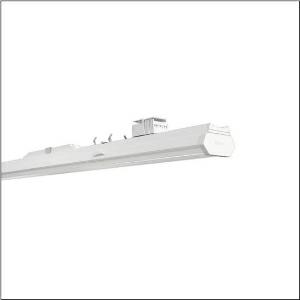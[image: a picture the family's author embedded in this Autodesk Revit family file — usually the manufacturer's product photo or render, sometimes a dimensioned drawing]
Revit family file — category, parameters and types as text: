
# Revit family: licross_r__21_protected_mo_52td11cn49xg_2815
name_source: partatom
category: Lighting Fixtures
units: mm (PartAtom-declared; Revit-internal decimal feet)

## family parameters
Cut with Voids When Loaded = No
Host = Face
Light Source = No
Part Type = Normal
Room Calculation Point = No
Round Connector Dimension = Use Diameter
Shared = No

## types (1)
- --- (1 x LED, 9070 lm, 50.4 W, 4000K)
    Apparent Load = 50 VA
    CIE Flux Codes = 83 94 98 100 100
    Color Rendering = 80
    Color Temperature = 4000K
    Default Elevation = 1800 mm
    Description = Licross® 21 Protected MO, luminaire insert, of sheet steel, galvanised, coil coated, white, length: 1.500mm, width: 90mm, height: 103mm, LED rated luminous flux: 9.080lm, light colour: 840, control gear: ON/OFF Multilumen, CLOi, control gear: ECG Multilumen, with plug, 3-pole, with phase selection, mains connection: 220..240V, AC, 50/60Hz, start of lifetime: 50W, end of service life: 61W, internal wiring halogen-free, primary light control with lens, of plastic, primary optical cover: cover, of PMMA, light emission: direct distribution, primary light characteristic: symmetric, protection rating (complete): IP54, insulation class (complete): insulation class I (protective earthing), certification: CE, ENEC, VDE, UKCA, protection symbol: D if used in an environment with non-conductive dust loads with corresponding accessories, impact resistance: IK06, permissible ambient temperature for indoor applications: -35..+45°C, corresponds to IFS (International Featured Standards) requirements for safety and quality in the food industry, reducing of maximum allowable ambient temperature of 5°C with ceiling mounting, LABS conformity tested according to VDMA 24364:2018-05, packaging unit: 1 piece
    Height = 92 mm
    Lamp = 1 x LED
    Lamp Light Flux = 9070 lm
    Lamp Power = 50.4 W
    Lamp count = 1
    Length = 1500 mm
    Luminous efficacy = 180 lm/W
    Manufacturer = Siteco
    ModVariant = No
    Model = 52TD11CN49XG
    Mounting Place = Ceiling
    Mounting Type = Pendant
    Number of Poles = 1
    OnlyDefault = Yes
    Power Factor = 1
    Product Name = Licross® 21 Protected MO
    Product group = luminaire insert | ceiling pendant
    ProductGroupID = 902
    Protection Class = Protection class I
    Protection Degree = IP 54
    RLX_Detail_Level = 1
    RLX_Emergency_Light_Flux = 0 lm
    RLX_Emergency_Type = 0
    RLX_Emergency_Type_DB = No
    RlxData = <blob elided: 21977 chars, md5=77095977>
    Socket = socket
    Standby Power = 0 W
    System Light Flux = 9070 lm
    System Power = 50 W
    Type Comments = factory setting: luminous flux: 100 % | (A | C | E) | 117 mA
    Type Image = l_1256148.jpg
    URL = http://relux.com
    VarID = @adj_132355
    Voltage = 0 V
    Weight = 0.00 kg
    Width = 88 mm

## geometry (parser evidence)
native form markers: Blend x4, Sweep x10
no freeform markers — native parametric forms only
